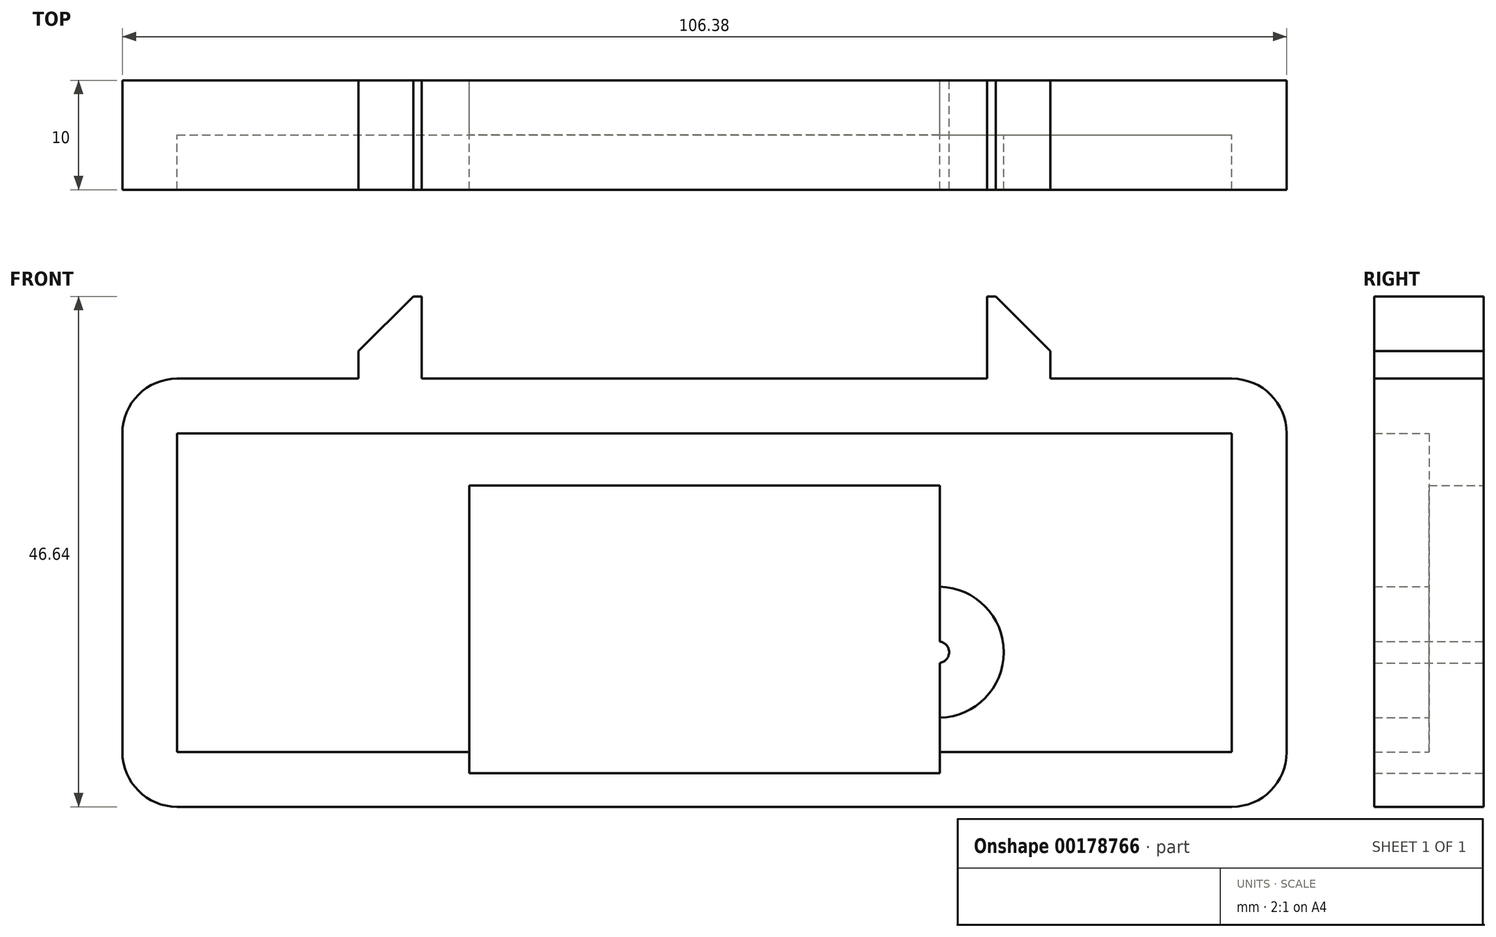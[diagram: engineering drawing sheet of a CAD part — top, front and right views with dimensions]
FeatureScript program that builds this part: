
annotation { "Feature Type Name" : "Feature", "Feature Type Description" : "" }
export const myFeature = defineFeature(function(context is Context, id is Id, definition is map)
    precondition{}
    {
        {
            var Q0;
            Q0=qCreatedBy(makeId("Front.planeOp"),FACE);
            var sketch = newSketch(context, id + "F0", { "sketchPlane" : qUnion([Q0])});
            skLineSegment(sketch, "E0", {"start": v(0, 0) * mm, "end": v(25.82, 0) * mm});
            skLineSegment(sketch, "E1", {"start": v(25.82, 0) * mm, "end": v(25.82, 7.52) * mm});
            skLineSegment(sketch, "E2", {"start": v(25.82, 7.52) * mm, "end": v(31.6, 7.52) * mm});
            skLineSegment(sketch, "E3", {"start": v(31.6, 7.52) * mm, "end": v(31.6, 0) * mm});
            skLineSegment(sketch, "E4", {"start": v(31.6, 0) * mm, "end": v(48.19, 0) * mm});
            skLineSegment(sketch, "E5", {"start": v(53.19, -5) * mm, "end": v(53.19, -34.12) * mm});
            skLineSegment(sketch, "E6", {"start": v(48.19, -39.12) * mm, "end": v(0, -39.12) * mm});
            skLineSegment(sketch, "E7.MirrorCS", {"start": v(0, 0) * mm, "end": v(-25.82, 0) * mm});
            skLineSegment(sketch, "E8.MirrorCS", {"start": v(-25.82, 0) * mm, "end": v(-25.82, 7.52) * mm});
            skLineSegment(sketch, "E9.MirrorCS", {"start": v(-25.82, 7.52) * mm, "end": v(-31.6, 7.52) * mm});
            skLineSegment(sketch, "E10.MirrorCS", {"start": v(-31.6, 7.52) * mm, "end": v(-31.6, 0) * mm});
            skLineSegment(sketch, "E11.MirrorCS", {"start": v(-31.6, 0) * mm, "end": v(-48.19, 0) * mm});
            skLineSegment(sketch, "E12.MirrorCS", {"start": v(-53.19, -5) * mm, "end": v(-53.19, -34.12) * mm});
            skLineSegment(sketch, "E13.MirrorCS", {"start": v(-48.19, -39.12) * mm, "end": v(0, -39.12) * mm});
            skPoint(sketch, "E14.visualSharp", {"position": v(53.19, 0) * mm});
            skArc(sketch, "E14.filletArc", {"start": v(53.19, -5) * mm, "mid": v(51.72, -1.46) * mm, "end": v(48.19, 0) * mm});
            skPoint(sketch, "E15.visualSharp", {"position": v(-53.19, 0) * mm});
            skArc(sketch, "E15.filletArc", {"start": v(-48.19, 0) * mm, "mid": v(-51.72, -1.46) * mm, "end": v(-53.19, -5) * mm});
            skPoint(sketch, "E16.visualSharp", {"position": v(-53.19, -39.12) * mm});
            skArc(sketch, "E16.filletArc", {"start": v(-53.19, -34.12) * mm, "mid": v(-51.72, -37.66) * mm, "end": v(-48.19, -39.12) * mm});
            skPoint(sketch, "E17.visualSharp", {"position": v(53.19, -39.12) * mm});
            skArc(sketch, "E17.filletArc", {"start": v(48.19, -39.12) * mm, "mid": v(51.72, -37.66) * mm, "end": v(53.19, -34.12) * mm});
            skPoint(sketch, "E18.middle", {"position": v(0, -20.6) * mm});
            skCircle(sketch, "E19", {"center": v(21.36, -25) * mm, "radius": 0.98 * mm});
            skSolve(sketch);
        }
        {
            var Q0;
            Q0=makeQuery(id+"F0.imprint","IMPRINT",FACE,{"disambiguationData":[TD([[makeQuery(id+"F0.imprint","IMPRINT",EDGE,{"derivedFrom":sQuery(id+"F0.wireOp",EDGE,"E0")}),-1.0]])]});
            extrude(context, id + "F1", {"entities" : qUnion([Q0]), "depth" : 10 * mm});
        }
        {
            var Q0;
            Q0=makeQuery(id+"F1.opExtrude","CAP_FACE",FACE,{"disambiguationData":[OSD([sQuery(id+"F0.wireOp",EDGE,"E0"),sQuery(id+"F0.wireOp",EDGE,"E1"),sQuery(id+"F0.wireOp",EDGE,"E2"),sQuery(id+"F0.wireOp",EDGE,"E3"),sQuery(id+"F0.wireOp",EDGE,"E4"),sQuery(id+"F0.wireOp",EDGE,"E5"),sQuery(id+"F0.wireOp",EDGE,"E6"),sQuery(id+"F0.wireOp",EDGE,"E7.MirrorCS"),sQuery(id+"F0.wireOp",EDGE,"E8.MirrorCS"),sQuery(id+"F0.wireOp",EDGE,"E9.MirrorCS"),sQuery(id+"F0.wireOp",EDGE,"E10.MirrorCS"),sQuery(id+"F0.wireOp",EDGE,"E11.MirrorCS"),sQuery(id+"F0.wireOp",EDGE,"E12.MirrorCS"),sQuery(id+"F0.wireOp",EDGE,"E13.MirrorCS"),sQuery(id+"F0.wireOp",EDGE,"E14.filletArc"),sQuery(id+"F0.wireOp",EDGE,"E15.filletArc"),sQuery(id+"F0.wireOp",EDGE,"E16.filletArc"),sQuery(id+"F0.wireOp",EDGE,"E17.filletArc"),sQuery(id+"F0.wireOp",EDGE,"E19")])],"isStart":false});
            shell(context, id + "F2", {"entities" : qUnion([Q0]), "thickness" : 5 * mm});
        }
        {
            var Q0;
            Q0=makeQuery(id+"F1.opExtrude","SWEPT_EDGE",EDGE,{"disambiguationData":[OSD([sQuery(id+"F0.wireOp",EDGE,"E9.MirrorCS"),sQuery(id+"F0.wireOp",EDGE,"E10.MirrorCS")])]});
            var Q1;
            Q1=makeQuery(id+"F1.opExtrude","SWEPT_EDGE",EDGE,{"disambiguationData":[OSD([sQuery(id+"F0.wireOp",EDGE,"E2"),sQuery(id+"F0.wireOp",EDGE,"E3")])]});
            chamfer(context, id + "F3", {"entities" : qUnion([Q0, Q1]), "width" : 5 * mm, "tangentPropagation" : true});
        }
        {
            var Q0;
            Q0=makeQuery(id+"F1.opExtrude","CAP_FACE",FACE,{"disambiguationData":[OSD([sQuery(id+"F0.wireOp",EDGE,"E0"),sQuery(id+"F0.wireOp",EDGE,"E1"),sQuery(id+"F0.wireOp",EDGE,"E2"),sQuery(id+"F0.wireOp",EDGE,"E3"),sQuery(id+"F0.wireOp",EDGE,"E4"),sQuery(id+"F0.wireOp",EDGE,"E5"),sQuery(id+"F0.wireOp",EDGE,"E6"),sQuery(id+"F0.wireOp",EDGE,"E7.MirrorCS"),sQuery(id+"F0.wireOp",EDGE,"E8.MirrorCS"),sQuery(id+"F0.wireOp",EDGE,"E9.MirrorCS"),sQuery(id+"F0.wireOp",EDGE,"E10.MirrorCS"),sQuery(id+"F0.wireOp",EDGE,"E11.MirrorCS"),sQuery(id+"F0.wireOp",EDGE,"E12.MirrorCS"),sQuery(id+"F0.wireOp",EDGE,"E13.MirrorCS"),sQuery(id+"F0.wireOp",EDGE,"E14.filletArc"),sQuery(id+"F0.wireOp",EDGE,"E15.filletArc"),sQuery(id+"F0.wireOp",EDGE,"E16.filletArc"),sQuery(id+"F0.wireOp",EDGE,"E17.filletArc"),sQuery(id+"F0.wireOp",EDGE,"E19")])],"isStart":true});
            var sketch = newSketch(context, id + "F4", { "sketchPlane" : qUnion([Q0])});
            skLineSegment(sketch, "E20.bottom", {"start": v(21.5, -9.76) * mm, "end": v(-21.5, -9.76) * mm});
            skLineSegment(sketch, "E20.top", {"start": v(21.5, -36.06) * mm, "end": v(-21.5, -36.06) * mm});
            skLineSegment(sketch, "E20.left", {"start": v(21.5, -9.76) * mm, "end": v(21.5, -36.06) * mm});
            skLineSegment(sketch, "E20.right", {"start": v(-21.5, -9.76) * mm, "end": v(-21.5, -36.06) * mm});
            skPoint(sketch, "E20.middle", {"position": v(0, -22.9) * mm});
            skSolve(sketch);
        }
        {
            var Q0;
            {var subQ1=sQuery(id+"F4.wireOp",EDGE,"E20.bottom");Q0=makeQuery(id+"F4.imprint","IMPRINT",FACE,{"disambiguationData":[TD([[makeQuery(id+"F4.imprint","IMPRINT",EDGE,{"derivedFrom":subQ1}),1.0]])]});}
            extrude(context, id + "F5", {"entities" : qUnion([Q0]), "operationType" : NewBodyOperationType.REMOVE, "oppositeDirection" : true, "depth" : 25 * mm});
        }
    });
